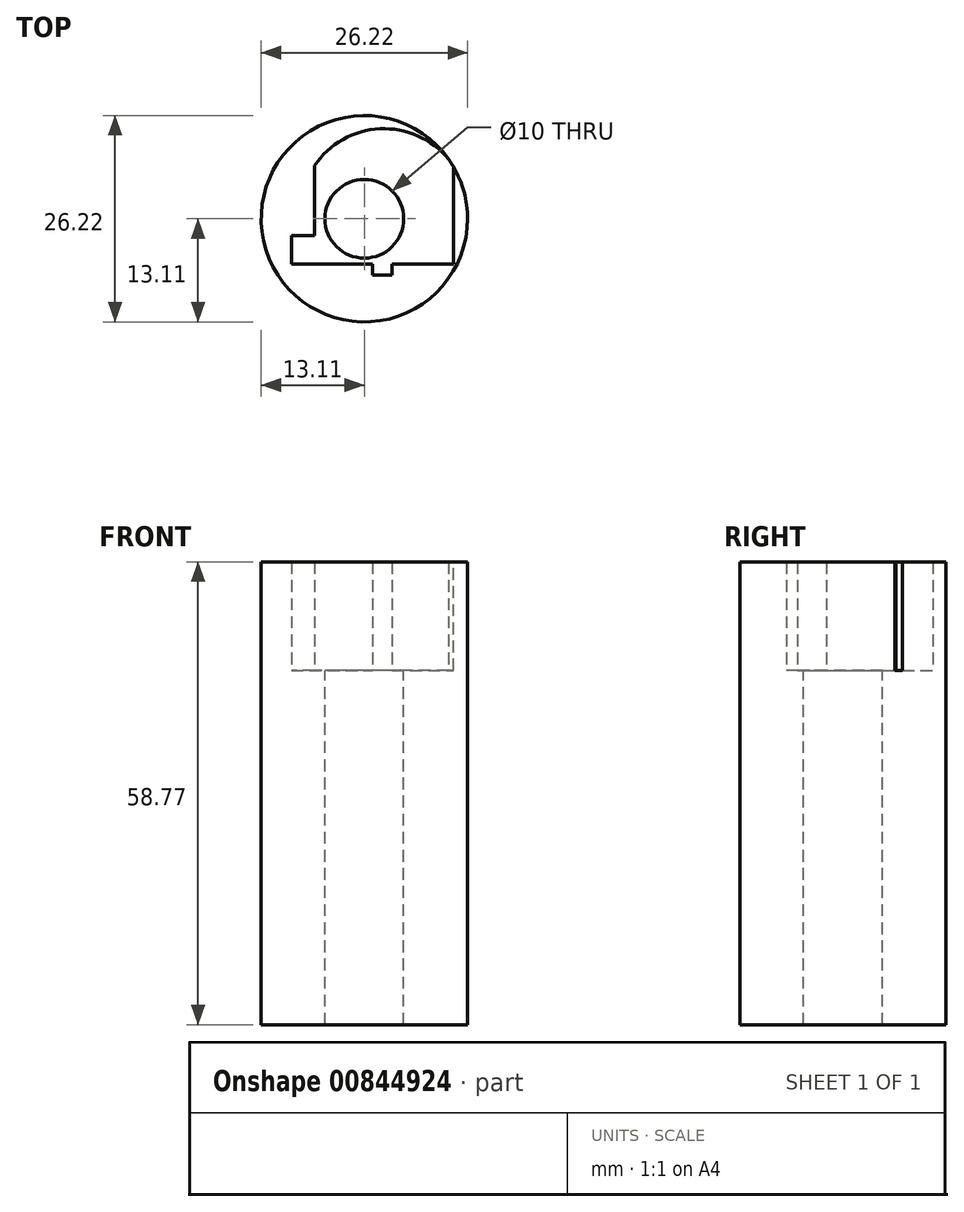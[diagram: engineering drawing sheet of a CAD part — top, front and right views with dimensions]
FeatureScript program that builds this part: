
annotation { "Feature Type Name" : "Feature", "Feature Type Description" : "" }
export const myFeature = defineFeature(function(context is Context, id is Id, definition is map)
    precondition{}
    {
        {
            var Q0;
            Q0=qCreatedBy(makeId("Top.planeOp"),FACE);
            var sketch = newSketch(context, id + "F0", { "sketchPlane" : qUnion([Q0])});
            skCircle(sketch, "E0", {"center": v(0, 0) * mm, "radius": 13.12 * mm, "construction": true});
            skSolve(sketch);
        }
        {
            var Q0;
            Q0=qCreatedBy(makeId("Top.planeOp"),FACE);
            var sketch = newSketch(context, id + "F1", { "sketchPlane" : qUnion([Q0])});
            skCircle(sketch, "E1", {"center": v(0, 0) * mm, "radius": 13.1 * mm});
            skCircle(sketch, "E2", {"center": v(0, 0) * mm, "radius": 5 * mm});
            skCircle(sketch, "E3.0", {"center": v(0, 0) * mm, "radius": 13.12 * mm});
            skSolve(sketch);
        }
        {
            var Q0;
            Q0=makeQuery(id+"F1.imprint","IMPRINT",FACE,{"disambiguationData":[TD([[makeQuery(id+"F1.imprint","IMPRINT",EDGE,{"derivedFrom":sQuery(id+"F1.wireOp",EDGE,"E1")}),1.0]])]});
            extrude(context, id + "F2", {"entities" : qUnion([Q0]), "oppositeDirection" : true, "depth" : 30 * mm, "offsetDistance" : 25 * mm, "hasSecondDirection" : true, "secondDirectionOppositeDirection" : false, "secondDirectionDepth" : 28.77 * mm});
        }
        {
            var Q0;
            Q0=qCreatedBy(makeId("Top.planeOp"),FACE);
            cPlane(context, id + "F3", {"entities" : qUnion([Q0]), "cplaneType" : CPlaneType.OFFSET, "offset" : 15 * mm, "width" : 150 * mm, "height" : 150 * mm});
        }
        {
            var Q0;
            Q0=qCreatedBy(id+"F3.planeOp",FACE);
            var sketch = newSketch(context, id + "F4", { "sketchPlane" : qUnion([Q0])});
            skLineSegment(sketch, "E4.bottom", {"start": v(-9.28, -3.55) * mm, "end": v(11.32, -3.55) * mm});
            skLineSegment(sketch, "E4.top", {"start": v(-9.28, -5.76) * mm, "end": v(11.32, -5.76) * mm});
            skLineSegment(sketch, "E4.left", {"start": v(-9.28, -3.55) * mm, "end": v(-9.28, -5.76) * mm});
            skLineSegment(sketch, "E4.right", {"start": v(11.32, -3.55) * mm, "end": v(11.32, -5.76) * mm});
            skLineSegment(sketch, "E5.0", {"start": v(-6.34, -5.76) * mm, "end": v(1.01, -5.76) * mm});
            skLineSegment(sketch, "E6.top", {"start": v(3.52, -7.17) * mm, "end": v(1.01, -7.17) * mm});
            skLineSegment(sketch, "E6.left", {"start": v(3.52, -5.76) * mm, "end": v(3.52, -7.17) * mm});
            skLineSegment(sketch, "E6.right", {"start": v(1.01, -5.76) * mm, "end": v(1.01, -7.17) * mm});
            skLineSegment(sketch, "E7.0", {"start": v(10.91, -3.55) * mm, "end": v(10.91, -5.76) * mm});
            skLineSegment(sketch, "E8.0", {"start": v(-9.69, -3.55) * mm, "end": v(-9.69, -5.76) * mm});
            skLineSegment(sketch, "E9.top", {"start": v(-9.69, -8.47) * mm, "end": v(-6.34, -8.47) * mm});
            skLineSegment(sketch, "E9.left", {"start": v(-9.69, -5.76) * mm, "end": v(-9.69, -8.47) * mm});
            skLineSegment(sketch, "E9.right", {"start": v(-6.34, -5.76) * mm, "end": v(-6.34, -8.47) * mm});
            skLineSegment(sketch, "E10.trimOffspring", {"start": v(3.52, -5.76) * mm, "end": v(10.91, -5.76) * mm});
            skLineSegment(sketch, "E11.bottom", {"start": v(-6.34, -3.55) * mm, "end": v(-9.28, -3.55) * mm});
            skLineSegment(sketch, "E11.top", {"start": v(-6.34, -2.11) * mm, "end": v(-9.28, -2.11) * mm});
            skLineSegment(sketch, "E11.left", {"start": v(-6.34, -3.55) * mm, "end": v(-6.34, -2.11) * mm});
            skLineSegment(sketch, "E11.right", {"start": v(-9.28, -3.55) * mm, "end": v(-9.28, -2.11) * mm});
            skLineSegment(sketch, "E12.bottom", {"start": v(11.32, -3.55) * mm, "end": v(-6.34, -3.55) * mm});
            skLineSegment(sketch, "E12.top", {"start": v(11.32, 6.73) * mm, "end": v(-6.34, 6.73) * mm});
            skLineSegment(sketch, "E12.left", {"start": v(11.32, -3.55) * mm, "end": v(11.32, 6.73) * mm});
            skLineSegment(sketch, "E12.right", {"start": v(-6.34, -3.55) * mm, "end": v(-6.34, 6.73) * mm});
            skArc(sketch, "E13", {"start": v(11.32, 6.73) * mm, "mid": v(2.5, 11.44) * mm, "end": v(-6.34, 6.73) * mm});
            skSolve(sketch);
        }
        {
            var Q0;
            {var subQ1=sQuery(id+"F4.wireOp",EDGE,"E4.right");var subQ9=sQuery(id+"F4.wireOp",EDGE,"E11.left");var subQ12=sQuery(id+"F4.wireOp",EDGE,"E4.left");var subQ14=makeQuery(id+"F4.imprint","IMPRINT",EDGE,{"derivedFrom":subQ9});var subQ15=makeQuery(id+"F4.imprint","IMPRINT",EDGE,{"derivedFrom":sQuery(id+"F4.wireOp",EDGE,"E12.top")});Q0=qUnion([makeQuery(id+"F4.imprint","IMPRINT",FACE,{"disambiguationData":[TD([[makeQuery(id+"F4.imprint","IMPRINT",EDGE,{"derivedFrom":sQuery(id+"F4.wireOp",EDGE,"E6.top")}),-1.0]])]}),makeQuery(id+"F4.imprint","IMPRINT",FACE,{"disambiguationData":[TD([[makeQuery(id+"F4.imprint","IMPRINT",EDGE,{"derivedFrom":subQ12}),1.0]])]}),makeQuery(id+"F4.imprint","IMPRINT",FACE,{"disambiguationData":[TD([[subQ15,-1.0]])]}),makeQuery(id+"F4.imprint","IMPRINT",FACE,{"disambiguationData":[TD([[subQ14,-1.0]])]}),makeQuery(id+"F4.imprint","IMPRINT",FACE,{"disambiguationData":[TD([[makeQuery(id+"F4.imprint","IMPRINT",EDGE,{"derivedFrom":sQuery(id+"F4.wireOp",EDGE,"E11.top")}),1.0]])]}),makeQuery(id+"F4.imprint","IMPRINT",FACE,{"disambiguationData":[TD([[makeQuery(id+"F4.imprint","IMPRINT",EDGE,{"derivedFrom":subQ1}),-1.0]])]})]);}
            extrude(context, id + "F5", {"entities" : qUnion([Q0]), "operationType" : NewBodyOperationType.REMOVE, "depth" : 28.77 * mm, "offsetDistance" : 25 * mm});
        }
    });
